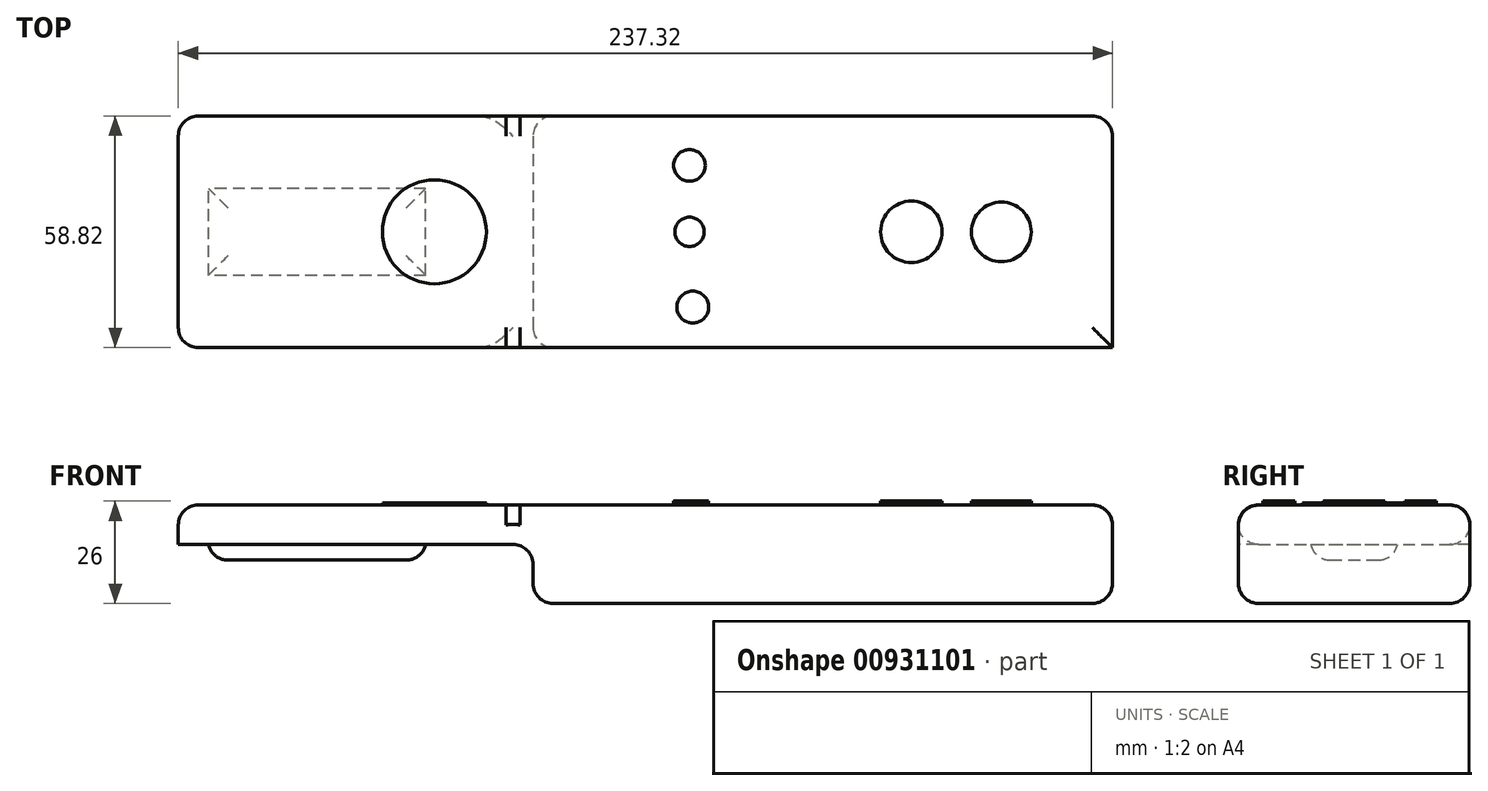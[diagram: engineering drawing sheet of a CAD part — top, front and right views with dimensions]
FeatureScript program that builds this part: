
annotation { "Feature Type Name" : "Feature", "Feature Type Description" : "" }
export const myFeature = defineFeature(function(context is Context, id is Id, definition is map)
    precondition{}
    {
        {
            var Q0;
            Q0=qCreatedBy(makeId("Top.planeOp"),FACE);
            var sketch = newSketch(context, id + "F0", { "sketchPlane" : qUnion([Q0])});
            skLineSegment(sketch, "E0.bottom", {"start": v(118.66, -29.4) * mm, "end": v(-118.66, -29.4) * mm});
            skLineSegment(sketch, "E0.top", {"start": v(118.66, 29.4) * mm, "end": v(-118.66, 29.4) * mm});
            skLineSegment(sketch, "E0.left", {"start": v(118.66, -29.4) * mm, "end": v(118.66, 29.4) * mm});
            skLineSegment(sketch, "E0.right", {"start": v(-118.66, -29.4) * mm, "end": v(-118.66, 29.4) * mm});
            skPoint(sketch, "E0.middle", {"position": v(0, 0) * mm});
            skSolve(sketch);
        }
        {
            var Q0;
            Q0=qSketchRegion(id+"F0",true);
            extrude(context, id + "F1", {"entities" : qUnion([Q0]), "depth" : 10 * mm});
        }
        {
            var Q0;
            Q0=makeQuery(id+"F1.opExtrude","CAP_FACE",FACE,{"disambiguationData":[OSD([sQuery(id+"F0.wireOp",EDGE,"E0.bottom"),sQuery(id+"F0.wireOp",EDGE,"E0.top"),sQuery(id+"F0.wireOp",EDGE,"E0.left"),sQuery(id+"F0.wireOp",EDGE,"E0.right")])],"isStart":true});
            var sketch = newSketch(context, id + "F2", { "sketchPlane" : qUnion([Q0])});
            skLineSegment(sketch, "E1.bottom", {"start": v(118.66, -29.4) * mm, "end": v(-28.54, -29.4) * mm});
            skLineSegment(sketch, "E1.top", {"start": v(118.66, 29.4) * mm, "end": v(-28.54, 29.4) * mm});
            skLineSegment(sketch, "E1.left", {"start": v(118.66, -29.4) * mm, "end": v(118.66, 29.4) * mm});
            skLineSegment(sketch, "E1.right", {"start": v(-28.54, -29.4) * mm, "end": v(-28.54, 29.4) * mm});
            skPoint(sketch, "E1.middle", {"position": v(45.06, 0) * mm});
            skSolve(sketch);
        }
        {
            var Q0;
            Q0=makeQuery(id+"F2.imprint","IMPRINT",FACE,{"disambiguationData":[TD([[makeQuery(id+"F2.imprint","IMPRINT",EDGE,{"derivedFrom":sQuery(id+"F2.wireOp",EDGE,"E1.bottom")}),-1.0]])]});
            extrude(context, id + "F3", {"entities" : qUnion([Q0]), "operationType" : NewBodyOperationType.ADD, "depth" : 15 * mm});
        }
        {
            var Q0;
            Q0=makeQuery(id+"F3.opExtrude","SWEPT_FACE",FACE,{"disambiguationData":[OSD([sQuery(id+"F2.wireOp",EDGE,"E1.right")])]});
            var Q1;
            Q1=makeQuery(id+"F3.opExtrude","CAP_FACE",FACE,{"disambiguationData":[OSD([sQuery(id+"F2.wireOp",EDGE,"E1.bottom"),sQuery(id+"F2.wireOp",EDGE,"E1.top"),sQuery(id+"F2.wireOp",EDGE,"E1.left"),sQuery(id+"F2.wireOp",EDGE,"E1.right")])],"isStart":false});
            fillet(context, id + "F4", {"entities" : qUnion([Q0, Q1]), "radius" : 5.08 * mm, "tangentPropagation" : true, "allowEdgeOverflow" : false});
        }
        {
            var Q0;
            Q0=makeQuery(id+"F1.opExtrude","CAP_FACE",FACE,{"disambiguationData":[OSD([sQuery(id+"F0.wireOp",EDGE,"E0.bottom"),sQuery(id+"F0.wireOp",EDGE,"E0.top"),sQuery(id+"F0.wireOp",EDGE,"E0.left"),sQuery(id+"F0.wireOp",EDGE,"E0.right")])],"isStart":true});
            var sketch = newSketch(context, id + "F5", { "sketchPlane" : qUnion([Q0])});
            skLineSegment(sketch, "E2.bottom", {"start": v(-55.8, 11.04) * mm, "end": v(-111, 11.04) * mm});
            skLineSegment(sketch, "E2.top", {"start": v(-55.8, -11.04) * mm, "end": v(-111, -11.04) * mm});
            skLineSegment(sketch, "E2.left", {"start": v(-55.8, 11.04) * mm, "end": v(-55.8, -11.04) * mm});
            skLineSegment(sketch, "E2.right", {"start": v(-111, 11.04) * mm, "end": v(-111, -11.04) * mm});
            skPoint(sketch, "E2.middle", {"position": v(-83.4, 0) * mm});
            skSolve(sketch);
        }
        {
            var Q0;
            Q0=qSketchRegion(id+"F5",true);
            extrude(context, id + "F6", {"entities" : qUnion([Q0]), "operationType" : NewBodyOperationType.ADD, "depth" : 4 * mm});
        }
        {
            var Q0;
            Q0=makeQuery(id+"F6.opExtrude","CAP_FACE",FACE,{"disambiguationData":[OSD([sQuery(id+"F5.wireOp",EDGE,"E2.bottom"),sQuery(id+"F5.wireOp",EDGE,"E2.top"),sQuery(id+"F5.wireOp",EDGE,"E2.left"),sQuery(id+"F5.wireOp",EDGE,"E2.right")])],"isStart":false});
            fillet(context, id + "F7", {"entities" : qUnion([Q0]), "radius" : 5.08 * mm, "tangentPropagation" : true, "allowEdgeOverflow" : false});
        }
        {
            var Q0;
            Q0=makeQuery(id+"F1.opExtrude","CAP_FACE",FACE,{"disambiguationData":[OSD([sQuery(id+"F0.wireOp",EDGE,"E0.bottom"),sQuery(id+"F0.wireOp",EDGE,"E0.top"),sQuery(id+"F0.wireOp",EDGE,"E0.left"),sQuery(id+"F0.wireOp",EDGE,"E0.right")])],"isStart":false});
            var sketch = newSketch(context, id + "F8", { "sketchPlane" : qUnion([Q0])});
            skSolve(sketch);
        }
        {
            var Q0;
            Q0=makeQuery(id+"F8.imprint","IMPRINT",FACE,{"disambiguationData":[TD([[makeQuery(id+"F8.imprint","IMPRINT",EDGE,{"derivedFrom":makeQuery(id+"F1.opExtrude","CAP_EDGE",EDGE,{"disambiguationData":[OSD([sQuery(id+"F0.wireOp",EDGE,"E0.bottom")])],"isStart":false})}),-1.0]])]});
            var sketch = newSketch(context, id + "F9", { "sketchPlane" : qUnion([Q0])});
            skCircle(sketch, "E3", {"center": v(-53.6, 0) * mm, "radius": 13.21 * mm});
            skSolve(sketch);
        }
        {
            var Q0;
            Q0=makeQuery(id+"F9.imprint","IMPRINT",FACE,{"disambiguationData":[TD([[makeQuery(id+"F9.imprint","IMPRINT",EDGE,{"derivedFrom":sQuery(id+"F9.wireOp",EDGE,"E3")}),1.0]])]});
            extrude(context, id + "F10", {"entities" : qUnion([Q0]), "operationType" : NewBodyOperationType.ADD, "depth" : 0.5 * mm});
        }
        {
            var Q0;
            Q0=makeQuery(id+"F8.imprint","IMPRINT",FACE,{"disambiguationData":[TD([[makeQuery(id+"F8.imprint","IMPRINT",EDGE,{"derivedFrom":makeQuery(id+"F1.opExtrude","CAP_EDGE",EDGE,{"disambiguationData":[OSD([sQuery(id+"F0.wireOp",EDGE,"E0.bottom")])],"isStart":false})}),-1.0]])]});
            var sketch = newSketch(context, id + "F11", { "sketchPlane" : qUnion([Q0])});
            skCircle(sketch, "E4", {"center": v(-111.84, -23.08) * mm, "radius": 3.42 * mm});
            skSolve(sketch);
        }
        {
            var Q0;
            Q0=makeQuery(id+"F10.opExtrude","CAP_FACE",FACE,{"disambiguationData":[OSD([sQuery(id+"F9.wireOp",EDGE,"E3")])],"isStart":false});
            var sketch = newSketch(context, id + "F12", { "sketchPlane" : qUnion([Q0])});
            skCircle(sketch, "E5", {"center": v(12.05, -19.12) * mm, "radius": 4.05 * mm});
            skCircle(sketch, "E6", {"center": v(11.2, 0) * mm, "radius": 3.73 * mm});
            skCircle(sketch, "E7", {"center": v(11.2, 16.88) * mm, "radius": 4.02 * mm});
            skCircle(sketch, "E8", {"center": v(67.58, 0) * mm, "radius": 7.8 * mm});
            skCircle(sketch, "E9", {"center": v(90.44, 0) * mm, "radius": 7.58 * mm});
            skSolve(sketch);
        }
        {
            var Q0;
            Q0=qSketchRegion(id+"F12",true);
            extrude(context, id + "F13", {"entities" : qUnion([Q0]), "depth" : 0.5 * mm});
        }
        {
            var Q0;
            Q0=makeQuery(id+"F1.opExtrude","CAP_EDGE",EDGE,{"disambiguationData":[OSD([sQuery(id+"F0.wireOp",EDGE,"E0.top")])],"isStart":false});
            fillet(context, id + "F14", {"entities" : qUnion([Q0]), "radius" : 5.08 * mm, "tangentPropagation" : true, "allowEdgeOverflow" : false});
        }
        {
            var Q0;
            Q0=makeQuery(id+"F1.opExtrude","CAP_EDGE",EDGE,{"disambiguationData":[OSD([sQuery(id+"F0.wireOp",EDGE,"E0.left")])],"isStart":false});
            var Q1;
            Q1=makeQuery(id+"F1.opExtrude","CAP_EDGE",EDGE,{"disambiguationData":[OSD([sQuery(id+"F0.wireOp",EDGE,"E0.bottom")])],"isStart":false});
            fillet(context, id + "F15", {"entities" : qUnion([Q0, Q1]), "radius" : 5.08 * mm, "tangentPropagation" : true, "allowEdgeOverflow" : false});
        }
        {
            var Q0;
            Q0=makeQuery(id+"F1.opExtrude","CAP_EDGE",EDGE,{"disambiguationData":[OSD([sQuery(id+"F0.wireOp",EDGE,"E0.right")])],"isStart":false});
            fillet(context, id + "F16", {"entities" : qUnion([Q0]), "radius" : 5.08 * mm, "tangentPropagation" : true, "allowEdgeOverflow" : false});
        }
    });
